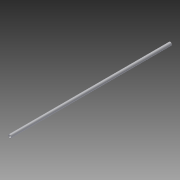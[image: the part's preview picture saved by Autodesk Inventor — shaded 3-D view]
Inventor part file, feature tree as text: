
AUTODESK INVENTOR PART (.ipt)
format: ipt  version: 2014 (Build 180170000, 170)  size: 68,096 bytes
history: native  units: in
note: dims shown in document units (in); Inventor stores cm internally (conversion verified against a paired STEP export)
features: extrude x1, sketch x1
ambient origin geometry x8: Origin, YZ Plane, XZ Plane, XY Plane, X Axis, Y Axis, Z Axis, Center Point
bodies: Solid1 (feature_tree)
feature tree (2):
  extrude  "Extrusion1"  Depth=120.0in
  sketch  "Sketch1"  dims[d0=2.375in d1=0.154in d2=120.0in d3=0.0in]
